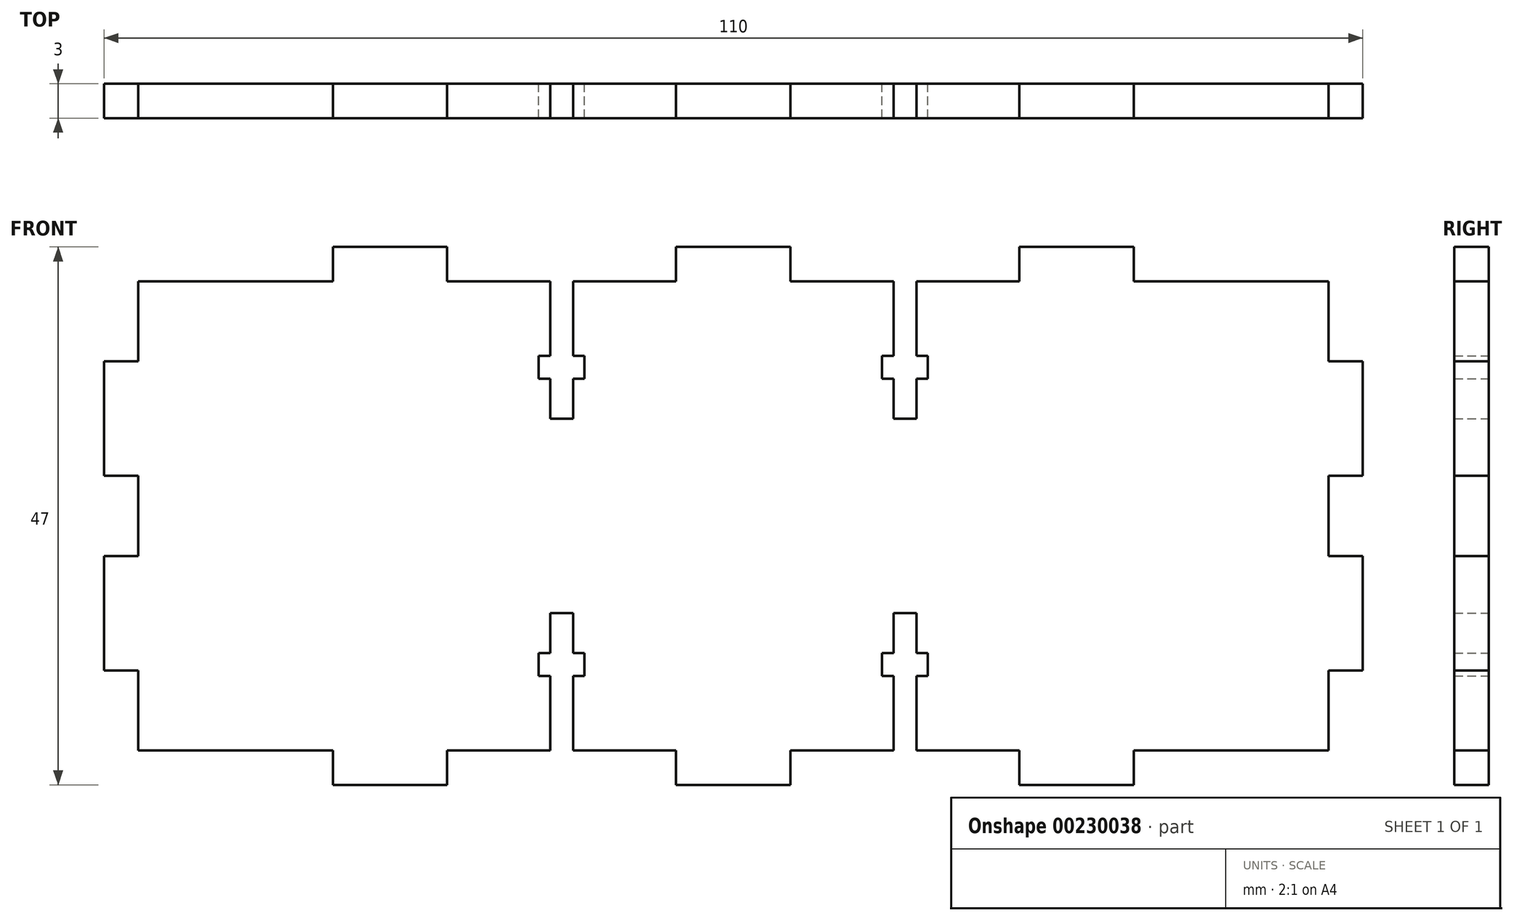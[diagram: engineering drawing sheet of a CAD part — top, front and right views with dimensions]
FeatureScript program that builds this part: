
annotation { "Feature Type Name" : "Feature", "Feature Type Description" : "" }
export const myFeature = defineFeature(function(context is Context, id is Id, definition is map)
    precondition{}
    {
        {
            var Q0;
            Q0=qCreatedBy(makeId("Front.planeOp"),FACE);
            var sketch = newSketch(context, id + "F0", { "sketchPlane" : qUnion([Q0])});
            skLineSegment(sketch, "E0", {"start": v(-56.01, 8.9) * mm, "end": v(-47.01, 8.9) * mm});
            skLineSegment(sketch, "E1", {"start": v(-47.01, 8.9) * mm, "end": v(-47.01, 2.4) * mm});
            skLineSegment(sketch, "E2", {"start": v(-47.01, 2.4) * mm, "end": v(-48.01, 2.4) * mm});
            skLineSegment(sketch, "E3", {"start": v(-48.01, 2.4) * mm, "end": v(-48.01, 0.4) * mm});
            skLineSegment(sketch, "E4", {"start": v(-48.01, 0.4) * mm, "end": v(-47.01, 0.4) * mm});
            skLineSegment(sketch, "E5", {"start": v(-47.01, 0.4) * mm, "end": v(-47.01, -3.1) * mm});
            skLineSegment(sketch, "E6", {"start": v(-47.01, -3.1) * mm, "end": v(-45.01, -3.1) * mm});
            skLineSegment(sketch, "E7", {"start": v(-45.01, -3.1) * mm, "end": v(-45.01, 0.4) * mm});
            skLineSegment(sketch, "E8", {"start": v(-45.01, 0.4) * mm, "end": v(-44.01, 0.4) * mm});
            skLineSegment(sketch, "E9", {"start": v(-44.01, 0.4) * mm, "end": v(-44.01, 2.4) * mm});
            skLineSegment(sketch, "E10", {"start": v(-44.01, 2.4) * mm, "end": v(-45.01, 2.4) * mm});
            skLineSegment(sketch, "E11", {"start": v(-45.01, 2.4) * mm, "end": v(-45.01, 8.9) * mm});
            skLineSegment(sketch, "E12", {"start": v(-45.01, 8.9) * mm, "end": v(-36.01, 8.9) * mm});
            skLineSegment(sketch, "E13", {"start": v(-36.01, 11.9) * mm, "end": v(-36.01, 8.9) * mm});
            skLineSegment(sketch, "E14", {"start": v(-36.01, 11.9) * mm, "end": v(-31.01, 11.9) * mm});
            skLineSegment(sketch, "E15", {"start": v(-56.01, 8.9) * mm, "end": v(-56.01, 11.9) * mm});
            skLineSegment(sketch, "E16", {"start": v(-56.01, 11.9) * mm, "end": v(-66.01, 11.9) * mm});
            skLineSegment(sketch, "E17", {"start": v(-66.01, 11.9) * mm, "end": v(-66.01, 8.9) * mm});
            skLineSegment(sketch, "E18", {"start": v(-66.01, 8.9) * mm, "end": v(-83.01, 8.9) * mm});
            skLineSegment(sketch, "E19", {"start": v(-83.01, 8.9) * mm, "end": v(-83.01, 1.9) * mm});
            skLineSegment(sketch, "E20", {"start": v(-83.01, 1.9) * mm, "end": v(-86.01, 1.9) * mm});
            skLineSegment(sketch, "E21", {"start": v(-86.01, 1.9) * mm, "end": v(-86.01, -8.1) * mm});
            skLineSegment(sketch, "E22", {"start": v(-86.01, -8.1) * mm, "end": v(-83.01, -8.1) * mm});
            skLineSegment(sketch, "E23", {"start": v(-83.01, -8.1) * mm, "end": v(-83.01, -11.6) * mm});
            skLineSegment(sketch, "E24", {"start": v(-83.01, -11.6) * mm, "end": v(-31.01, -11.6) * mm, "construction": true});
            skLineSegment(sketch, "E25.MirrorCS", {"start": v(-45.01, -23.6) * mm, "end": v(-44.01, -23.6) * mm});
            skLineSegment(sketch, "E26.MirrorCS", {"start": v(-44.01, -23.6) * mm, "end": v(-44.01, -25.6) * mm});
            skLineSegment(sketch, "E27.MirrorCS", {"start": v(-44.01, -25.6) * mm, "end": v(-45.01, -25.6) * mm});
            skLineSegment(sketch, "E28.MirrorCS", {"start": v(-47.01, -20.1) * mm, "end": v(-45.01, -20.1) * mm});
            skLineSegment(sketch, "E29.MirrorCS", {"start": v(-48.01, -23.6) * mm, "end": v(-47.01, -23.6) * mm});
            skLineSegment(sketch, "E30.MirrorCS", {"start": v(-47.01, -25.6) * mm, "end": v(-48.01, -25.6) * mm});
            skLineSegment(sketch, "E31.MirrorCS", {"start": v(-48.01, -25.6) * mm, "end": v(-48.01, -23.6) * mm});
            skLineSegment(sketch, "E32.MirrorCS", {"start": v(-86.01, -15.1) * mm, "end": v(-83.01, -15.1) * mm});
            skLineSegment(sketch, "E33.MirrorCS", {"start": v(-83.01, -25.1) * mm, "end": v(-86.01, -25.1) * mm});
            skLineSegment(sketch, "E34.MirrorCS", {"start": v(-47.01, -23.6) * mm, "end": v(-47.01, -20.1) * mm});
            skLineSegment(sketch, "E35.MirrorCS", {"start": v(-45.01, -20.1) * mm, "end": v(-45.01, -23.6) * mm});
            skLineSegment(sketch, "E36.MirrorCS", {"start": v(-56.01, -35.1) * mm, "end": v(-66.01, -35.1) * mm});
            skLineSegment(sketch, "E37.MirrorCS", {"start": v(-66.01, -32.1) * mm, "end": v(-83.01, -32.1) * mm});
            skLineSegment(sketch, "E38.MirrorCS", {"start": v(-47.01, -32.1) * mm, "end": v(-47.01, -25.6) * mm});
            skLineSegment(sketch, "E39.MirrorCS", {"start": v(-56.01, -32.1) * mm, "end": v(-47.01, -32.1) * mm});
            skLineSegment(sketch, "E40.MirrorCS", {"start": v(-56.01, -32.1) * mm, "end": v(-56.01, -35.1) * mm});
            skLineSegment(sketch, "E41.MirrorCS", {"start": v(-36.01, -35.1) * mm, "end": v(-31.01, -35.1) * mm});
            skLineSegment(sketch, "E42.MirrorCS", {"start": v(-36.01, -35.1) * mm, "end": v(-36.01, -32.1) * mm});
            skLineSegment(sketch, "E43.MirrorCS", {"start": v(-66.01, -35.1) * mm, "end": v(-66.01, -32.1) * mm});
            skLineSegment(sketch, "E44.MirrorCS", {"start": v(-83.01, -32.1) * mm, "end": v(-83.01, -25.1) * mm});
            skLineSegment(sketch, "E45.MirrorCS", {"start": v(-83.01, -15.1) * mm, "end": v(-83.01, -11.6) * mm});
            skLineSegment(sketch, "E46.MirrorCS", {"start": v(-45.01, -32.1) * mm, "end": v(-36.01, -32.1) * mm});
            skLineSegment(sketch, "E47.MirrorCS", {"start": v(-45.01, -25.6) * mm, "end": v(-45.01, -32.1) * mm});
            skLineSegment(sketch, "E48.MirrorCS", {"start": v(-86.01, -25.1) * mm, "end": v(-86.01, -15.1) * mm});
            skLineSegment(sketch, "E49", {"start": v(-31.01, 11.9) * mm, "end": v(-31.01, -35.1) * mm, "construction": true});
            skLineSegment(sketch, "E50.MirrorCS", {"start": v(-15.01, 2.4) * mm, "end": v(-14.01, 2.4) * mm});
            skLineSegment(sketch, "E51.MirrorCS", {"start": v(-17.01, 0.4) * mm, "end": v(-18.01, 0.4) * mm});
            skLineSegment(sketch, "E52.MirrorCS", {"start": v(-18.01, -25.6) * mm, "end": v(-17.01, -25.6) * mm});
            skLineSegment(sketch, "E53.MirrorCS", {"start": v(-14.01, -23.6) * mm, "end": v(-15.01, -23.6) * mm});
            skLineSegment(sketch, "E54.MirrorCS", {"start": v(-18.01, -23.6) * mm, "end": v(-18.01, -25.6) * mm});
            skLineSegment(sketch, "E55.MirrorCS", {"start": v(-14.01, 2.4) * mm, "end": v(-14.01, 0.4) * mm});
            skLineSegment(sketch, "E56.MirrorCS", {"start": v(-14.01, 0.4) * mm, "end": v(-15.01, 0.4) * mm});
            skLineSegment(sketch, "E57.MirrorCS", {"start": v(-15.01, -3.1) * mm, "end": v(-17.01, -3.1) * mm});
            skLineSegment(sketch, "E58.MirrorCS", {"start": v(-18.01, 0.4) * mm, "end": v(-18.01, 2.4) * mm});
            skLineSegment(sketch, "E59.MirrorCS", {"start": v(-18.01, 2.4) * mm, "end": v(-17.01, 2.4) * mm});
            skLineSegment(sketch, "E60.MirrorCS", {"start": v(-15.01, -20.1) * mm, "end": v(-17.01, -20.1) * mm});
            skLineSegment(sketch, "E61.MirrorCS", {"start": v(-15.01, -25.6) * mm, "end": v(-14.01, -25.6) * mm});
            skLineSegment(sketch, "E62.MirrorCS", {"start": v(-14.01, -25.6) * mm, "end": v(-14.01, -23.6) * mm});
            skLineSegment(sketch, "E63.MirrorCS", {"start": v(-17.01, -23.6) * mm, "end": v(-18.01, -23.6) * mm});
            skLineSegment(sketch, "E64.MirrorCS", {"start": v(-15.01, 0.4) * mm, "end": v(-15.01, -3.1) * mm});
            skLineSegment(sketch, "E65.MirrorCS", {"start": v(-15.01, -23.6) * mm, "end": v(-15.01, -20.1) * mm});
            skLineSegment(sketch, "E66.MirrorCS", {"start": v(-26.01, -35.1) * mm, "end": v(-26.01, -32.1) * mm});
            skLineSegment(sketch, "E67.MirrorCS", {"start": v(20.99, 8.9) * mm, "end": v(20.99, 1.9) * mm});
            skLineSegment(sketch, "E68.MirrorCS", {"start": v(-17.01, -20.1) * mm, "end": v(-17.01, -23.6) * mm});
            skLineSegment(sketch, "E69.MirrorCS", {"start": v(-26.01, 11.9) * mm, "end": v(-26.01, 8.9) * mm});
            skLineSegment(sketch, "E70.MirrorCS", {"start": v(-26.01, 11.9) * mm, "end": v(-31.01, 11.9) * mm});
            skLineSegment(sketch, "E71.MirrorCS", {"start": v(-6.01, 8.9) * mm, "end": v(-6.01, 11.9) * mm});
            skLineSegment(sketch, "E72.MirrorCS", {"start": v(-6.01, 8.9) * mm, "end": v(-15.01, 8.9) * mm});
            skLineSegment(sketch, "E73.MirrorCS", {"start": v(-15.01, 8.9) * mm, "end": v(-15.01, 2.4) * mm});
            skLineSegment(sketch, "E74.MirrorCS", {"start": v(-17.01, -3.1) * mm, "end": v(-17.01, 0.4) * mm});
            skLineSegment(sketch, "E75.MirrorCS", {"start": v(-17.01, 2.4) * mm, "end": v(-17.01, 8.9) * mm});
            skLineSegment(sketch, "E76.MirrorCS", {"start": v(3.99, -35.1) * mm, "end": v(3.99, -32.1) * mm});
            skLineSegment(sketch, "E77.MirrorCS", {"start": v(-17.01, 8.9) * mm, "end": v(-26.01, 8.9) * mm});
            skLineSegment(sketch, "E78.MirrorCS", {"start": v(-6.01, -32.1) * mm, "end": v(-15.01, -32.1) * mm});
            skLineSegment(sketch, "E79.MirrorCS", {"start": v(20.99, -8.1) * mm, "end": v(20.99, -11.6) * mm});
            skLineSegment(sketch, "E80.MirrorCS", {"start": v(20.99, 1.9) * mm, "end": v(23.99, 1.9) * mm});
            skLineSegment(sketch, "E81.MirrorCS", {"start": v(20.99, -15.1) * mm, "end": v(20.99, -11.6) * mm});
            skLineSegment(sketch, "E82.MirrorCS", {"start": v(20.99, -32.1) * mm, "end": v(20.99, -25.1) * mm});
            skLineSegment(sketch, "E83.MirrorCS", {"start": v(-6.01, -32.1) * mm, "end": v(-6.01, -35.1) * mm});
            skLineSegment(sketch, "E84.MirrorCS", {"start": v(20.99, -11.6) * mm, "end": v(-31.01, -11.6) * mm, "construction": true});
            skLineSegment(sketch, "E85.MirrorCS", {"start": v(23.99, 1.9) * mm, "end": v(23.99, -8.1) * mm});
            skLineSegment(sketch, "E86.MirrorCS", {"start": v(-17.01, -32.1) * mm, "end": v(-26.01, -32.1) * mm});
            skLineSegment(sketch, "E87.MirrorCS", {"start": v(20.99, -25.1) * mm, "end": v(23.99, -25.1) * mm});
            skLineSegment(sketch, "E88.MirrorCS", {"start": v(-15.01, -32.1) * mm, "end": v(-15.01, -25.6) * mm});
            skLineSegment(sketch, "E89.MirrorCS", {"start": v(-17.01, -25.6) * mm, "end": v(-17.01, -32.1) * mm});
            skLineSegment(sketch, "E90.MirrorCS", {"start": v(23.99, -8.1) * mm, "end": v(20.99, -8.1) * mm});
            skLineSegment(sketch, "E91.MirrorCS", {"start": v(-26.01, -35.1) * mm, "end": v(-31.01, -35.1) * mm});
            skLineSegment(sketch, "E92.MirrorCS", {"start": v(23.99, -15.1) * mm, "end": v(20.99, -15.1) * mm});
            skLineSegment(sketch, "E93.MirrorCS", {"start": v(23.99, -25.1) * mm, "end": v(23.99, -15.1) * mm});
            skLineSegment(sketch, "E94.MirrorCS", {"start": v(-6.01, -35.1) * mm, "end": v(3.99, -35.1) * mm});
            skLineSegment(sketch, "E95.MirrorCS", {"start": v(-6.01, 11.9) * mm, "end": v(3.99, 11.9) * mm});
            skLineSegment(sketch, "E96.MirrorCS", {"start": v(3.99, 8.9) * mm, "end": v(20.99, 8.9) * mm});
            skLineSegment(sketch, "E97.MirrorCS", {"start": v(3.99, 11.9) * mm, "end": v(3.99, 8.9) * mm});
            skLineSegment(sketch, "E98.MirrorCS", {"start": v(3.99, -32.1) * mm, "end": v(20.99, -32.1) * mm});
            skLineSegment(sketch, "E99", {"start": v(-61.01, 11.9) * mm, "end": v(-61.01, -35.1) * mm, "construction": true});
            skSolve(sketch);
        }
        {
            var Q0;
            Q0=makeQuery(id+"F0.imprint","IMPRINT",FACE,{"disambiguationData":[TD([[makeQuery(id+"F0.imprint","IMPRINT",EDGE,{"derivedFrom":sQuery(id+"F0.wireOp",EDGE,"E0")}),-1.0]])]});
            extrude(context, id + "F1", {"entities" : qUnion([Q0]), "depth" : 3 * mm});
        }
    });
